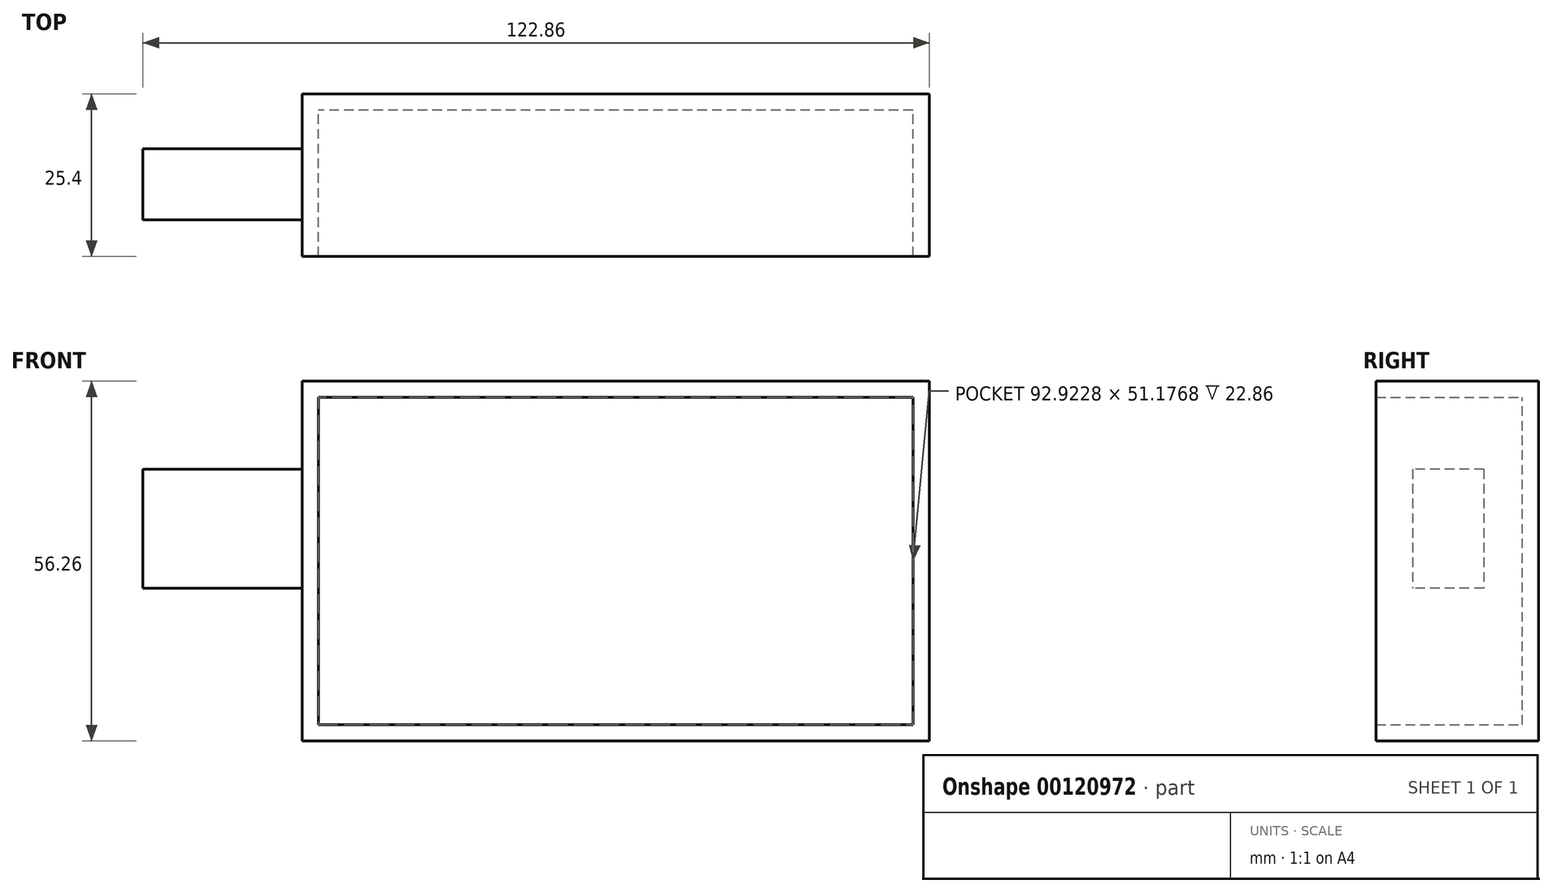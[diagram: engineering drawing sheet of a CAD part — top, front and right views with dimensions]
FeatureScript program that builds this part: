
annotation { "Feature Type Name" : "Feature", "Feature Type Description" : "" }
export const myFeature = defineFeature(function(context is Context, id is Id, definition is map)
    precondition{}
    {
        {
            var Q0;
            Q0=qCreatedBy(makeId("Front.planeOp"),FACE);
            var sketch = newSketch(context, id + "F0", { "sketchPlane" : qUnion([Q0])});
            skLineSegment(sketch, "E0.bottom", {"start": v(49, -28.13) * mm, "end": v(-49, -28.13) * mm});
            skLineSegment(sketch, "E0.top", {"start": v(49, 28.13) * mm, "end": v(-49, 28.13) * mm});
            skLineSegment(sketch, "E0.left", {"start": v(49, -28.13) * mm, "end": v(49, 28.13) * mm});
            skLineSegment(sketch, "E0.right", {"start": v(-49, -28.13) * mm, "end": v(-49, 28.13) * mm});
            skPoint(sketch, "E0.middle", {"position": v(0, 0) * mm});
            skSolve(sketch);
        }
        {
            var Q0;
            Q0 = qSketchRegion(id + "F0", true);
            extrude(context, id + "F1", {"entities" : qUnion([Q0]), "depth" : 25.4 * mm});
        }
        {
            var Q0;
            Q0=makeQuery(id+"F1.opExtrude","CAP_FACE",FACE,{"disambiguationData":[OSD([sQuery(id+"F0.wireOp",EDGE,"E0.bottom"),sQuery(id+"F0.wireOp",EDGE,"E0.top"),sQuery(id+"F0.wireOp",EDGE,"E0.left"),sQuery(id+"F0.wireOp",EDGE,"E0.right")])],"isStart":false});
            shell(context, id + "F2", {"entities" : qUnion([Q0]), "thickness" : 2.54 * mm});
        }
        {
            var Q0;
            Q0=makeQuery(id+"F2.opShell","OFFSET_FACE",FACE,{"disambiguationData":[OSD([sQuery(id+"F0.wireOp",EDGE,"E0.right")])]});
            var sketch = newSketch(context, id + "F3", { "sketchPlane" : qUnion([Q0])});
            skLineSegment(sketch, "E1.bottom", {"start": v(-19.71, -4.23) * mm, "end": v(-8.58, -4.23) * mm});
            skLineSegment(sketch, "E1.top", {"start": v(-19.71, 14.36) * mm, "end": v(-8.58, 14.36) * mm});
            skLineSegment(sketch, "E1.left", {"start": v(-19.71, -4.23) * mm, "end": v(-19.71, 14.36) * mm});
            skLineSegment(sketch, "E1.right", {"start": v(-8.58, -4.23) * mm, "end": v(-8.58, 14.36) * mm});
            skSolve(sketch);
        }
        {
            var Q0;
            Q0 = qSketchRegion(id + "F3", true);
            extrude(context, id + "F4", {"entities" : qUnion([Q0]), "operationType" : NewBodyOperationType.ADD, "oppositeDirection" : true, "depth" : 27.4 * mm});
        }
    });
